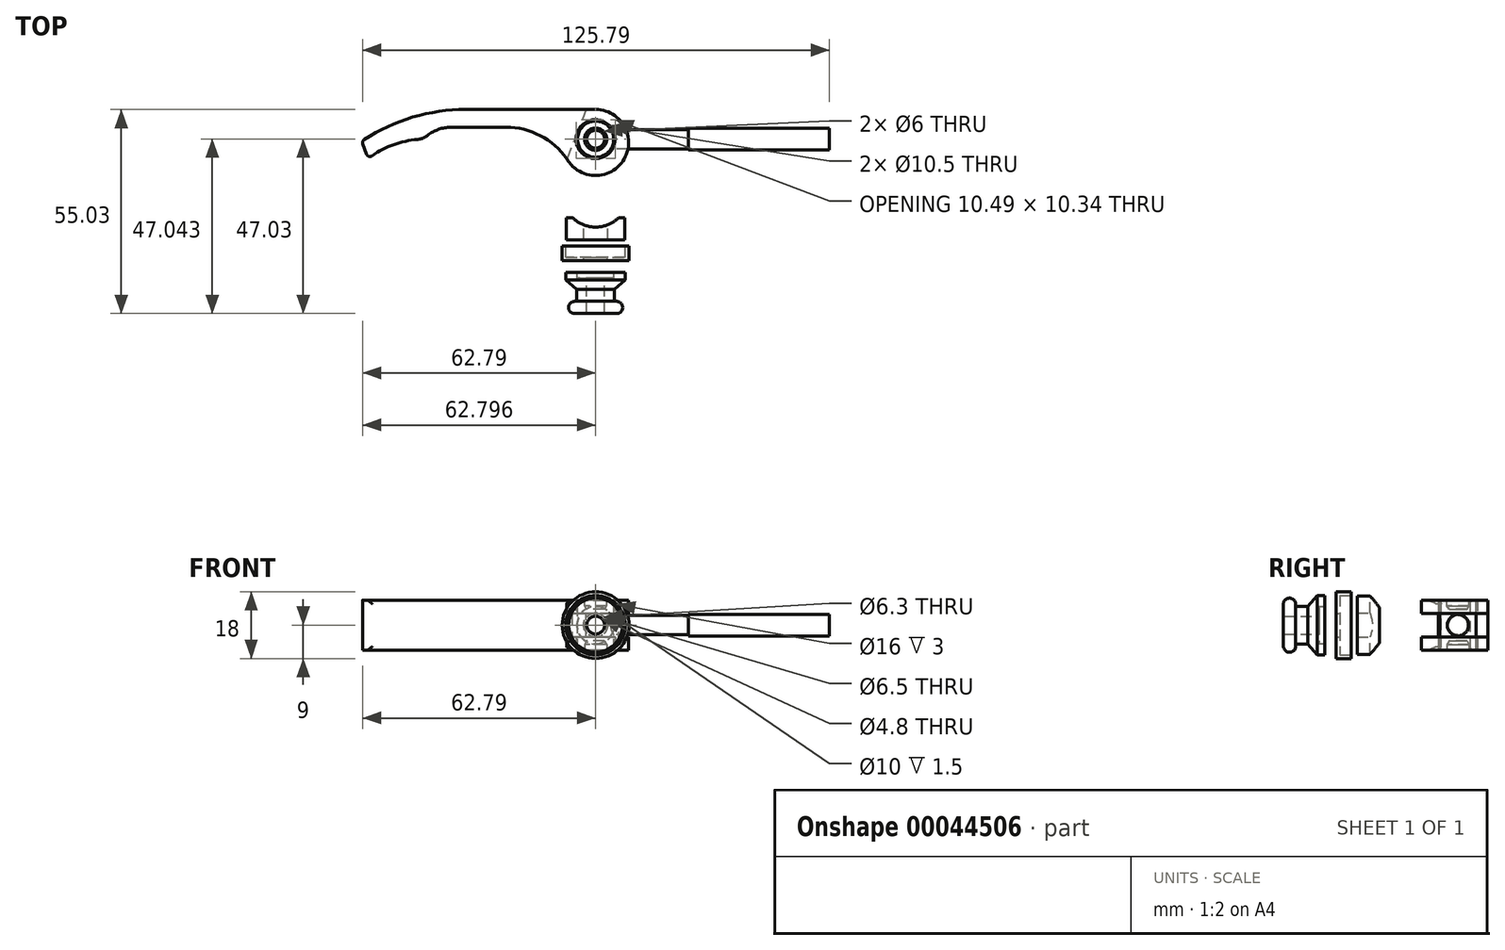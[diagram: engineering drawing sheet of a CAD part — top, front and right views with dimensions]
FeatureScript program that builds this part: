
annotation { "Feature Type Name" : "Feature", "Feature Type Description" : "" }
export const myFeature = defineFeature(function(context is Context, id is Id, definition is map)
    precondition{}
    {
        {
            var Q0;
            Q0=qCreatedBy(makeId("Top.planeOp"),FACE);
            var sketch = newSketch(context, id + "F0", { "sketchPlane" : qUnion([Q0])});
            skCircle(sketch, "E0", {"center": v(0, 0) * mm, "radius": 5.25 * mm});
            skCircle(sketch, "E1", {"center": v(0, -0.9) * mm, "radius": 8.9 * mm});
            skLineSegment(sketch, "E2", {"start": v(0, 8) * mm, "end": v(-35, 8) * mm});
            skArc(sketch, "E3", {"start": v(-35, 8) * mm, "mid": v(-49.64, 5.8) * mm, "end": v(-63, -0.58) * mm});
            skArc(sketch, "E4", {"start": v(-46.33, 0) * mm, "mid": v(-54.24, -1.42) * mm, "end": v(-61.29, -5.27) * mm});
            skArc(sketch, "E5", {"start": v(-39, 3.2) * mm, "mid": v(-43, 2.37) * mm, "end": v(-46.33, 0) * mm});
            skLineSegment(sketch, "E6", {"start": v(-63, -0.58) * mm, "end": v(-61.29, -5.27) * mm});
            skLineSegment(sketch, "E7", {"start": v(-39, 3.2) * mm, "end": v(-24.13, 3.2) * mm});
            skArc(sketch, "E8", {"start": v(-7.43, -5.8) * mm, "mid": v(-14.65, 0.8) * mm, "end": v(-24.13, 3.2) * mm});
            skLineSegment(sketch, "E9", {"start": v(-2.5, 8) * mm, "end": v(-7.74, -5.35) * mm});
            skSolve(sketch);
        }
        {
            var Q0;
            {var subQ0=sQuery(id+"F0.wireOp",EDGE,"E2");Q0=makeQuery(id+"F0.imprint","IMPRINT",FACE,{"disambiguationData":[TD([[makeQuery(id+"F0.imprint","IMPRINT",EDGE,{"derivedFrom":subQ0}),1.0]])]});}
            var Q1;
            Q1=makeQuery(id+"F0.imprint","IMPRINT",FACE,{"disambiguationData":[TD([[makeQuery(id+"F0.imprint","IMPRINT",EDGE,{"derivedFrom":sQuery(id+"F0.wireOp",EDGE,"E0")}),-1.0]])]});
            var Q2;
            {var subQ0=sQuery(id+"F0.wireOp",EDGE,"E9");var subQ1=sQuery(id+"F0.wireOp",EDGE,"E1");var subQ2=makeQuery(id+"F0.imprint","INTERSECT",VERTEX,{"disambiguationData":[OD(0.0)],"derivedFrom":[subQ1,subQ0]});Q2=makeQuery(id+"F0.imprint","IMPRINT",FACE,{"disambiguationData":[TD([[makeQuery(id+"F0.imprint","IMPRINT",EDGE,{"disambiguationData":[TD([[subQ2,-1.0]])],"derivedFrom":subQ1}),1.0]])]});}
            var Q3;
            {var subQ0=sQuery(id+"F0.wireOp",EDGE,"E3");Q3=makeQuery(id+"F0.imprint","IMPRINT",FACE,{"disambiguationData":[TD([[makeQuery(id+"F0.imprint","IMPRINT",EDGE,{"derivedFrom":subQ0}),1.0]])]});}
            extrude(context, id + "F1", {"entities" : qUnion([Q0, Q1, Q2, Q3]), "endBound" : BoundingType.SYMMETRIC, "depth" : 13.5 * mm});
        }
        {
            var Q0;
            {var subQ6=sQuery(id+"F0.wireOp",EDGE,"E0");Q0=makeQuery(id+"F0.imprint","IMPRINT",FACE,{"disambiguationData":[TD([[makeQuery(id+"F0.imprint","IMPRINT",EDGE,{"derivedFrom":subQ6}),-1.0]])]});}
            var Q1;
            Q1=makeQuery(id+"F0.imprint","IMPRINT",FACE,{"disambiguationData":[TD([[makeQuery(id+"F0.imprint","IMPRINT",EDGE,{"derivedFrom":sQuery(id+"F0.wireOp",EDGE,"E0")}),1.0]])]});
            var Q2;
            {var subQ0=sQuery(id+"F0.wireOp",EDGE,"E8");var subQ1=sQuery(id+"F0.wireOp",EDGE,"E1");var subQ2=makeQuery(id+"F0.imprint","INTERSECT",VERTEX,{"derivedFrom":[subQ1,subQ0]});Q2=makeQuery(id+"F0.imprint","IMPRINT",FACE,{"disambiguationData":[TD([[makeQuery(id+"F0.imprint","IMPRINT",EDGE,{"disambiguationData":[TD([[subQ2,1.0]])],"derivedFrom":subQ1}),-1.0]])]});}
            var Q3;
            {var subQ0=sQuery(id+"F0.wireOp",EDGE,"E2");var subQ1=sQuery(id+"F0.wireOp",EDGE,"E1");var subQ2=makeQuery(id+"F0.imprint","INTERSECT",VERTEX,{"derivedFrom":[subQ1,subQ0]});Q3=makeQuery(id+"F0.imprint","IMPRINT",FACE,{"disambiguationData":[TD([[makeQuery(id+"F0.imprint","IMPRINT",EDGE,{"disambiguationData":[TD([[subQ2,-1.0]])],"derivedFrom":subQ1}),-1.0]])]});}
            extrude(context, id + "F2", {"entities" : qUnion([Q0, Q1, Q2, Q3]), "operationType" : NewBodyOperationType.REMOVE, "endBound" : BoundingType.SYMMETRIC, "oppositeDirection" : true, "depth" : 6.4 * mm});
        }
        {
            var Q0;
            Q0=qCreatedBy(makeId("Front.planeOp"),FACE);
            var sketch = newSketch(context, id + "F3", { "sketchPlane" : qUnion([Q0])});
            skLineSegment(sketch, "E10", {"start": v(0, 14.1) * mm, "end": v(0, -21.5) * mm, "construction": true});
            skLineSegment(sketch, "E11", {"start": v(0, 0) * mm, "end": v(81.34, 0) * mm, "construction": true});
            skLineSegment(sketch, "E12.0", {"start": v(3, 6.75) * mm, "end": v(4.88, 6.75) * mm});
            skLineSegment(sketch, "E13", {"start": v(0, 4.25) * mm, "end": v(0, 0) * mm});
            skLineSegment(sketch, "E14", {"start": v(4.88, 0) * mm, "end": v(4.88, 6.75) * mm});
            skLineSegment(sketch, "E15", {"start": v(3, 6.75) * mm, "end": v(3, 5.25) * mm});
            skLineSegment(sketch, "E16", {"start": v(3, 5.25) * mm, "end": v(2.4, 4.25) * mm});
            skLineSegment(sketch, "E17", {"start": v(2.4, 4.25) * mm, "end": v(0, 4.25) * mm});
            skPoint(sketch, "E18.orphan", {"position": v(-7.73, 6.75) * mm});
            skPoint(sketch, "E19.orphan", {"position": v(8.9, 6.75) * mm});
            skLineSegment(sketch, "E20", {"start": v(0, 2.6) * mm, "end": v(25, 2.6) * mm});
            skLineSegment(sketch, "E21", {"start": v(25, 2.6) * mm, "end": v(25, 0) * mm});
            skLineSegment(sketch, "E22", {"start": v(25, 0) * mm, "end": v(0, 0) * mm});
            skLineSegment(sketch, "E23", {"start": v(25, 2.6) * mm, "end": v(25, 2.9) * mm});
            skLineSegment(sketch, "E24", {"start": v(25, 2.9) * mm, "end": v(63, 2.9) * mm});
            skLineSegment(sketch, "E25", {"start": v(63, 2.9) * mm, "end": v(63, 0) * mm});
            skLineSegment(sketch, "E26", {"start": v(63, 0) * mm, "end": v(25, 0) * mm});
            skSolve(sketch);
        }
        {
            var Q0;
            Q0=makeQuery(id+"F1.opExtrude","SWEPT_EDGE",EDGE,{"disambiguationData":[OSD([sQuery(id+"F0.wireOp",EDGE,"E4"),sQuery(id+"F0.wireOp",EDGE,"E5")])]});
            fillet(context, id + "F4", {"entities" : qUnion([Q0]), "radius" : 5 * mm, "tangentPropagation" : true, "allowEdgeOverflow" : false});
        }
        {
            var Q0;
            Q0=makeQuery(id+"F1.opExtrude","SWEPT_EDGE",EDGE,{"disambiguationData":[OSD([sQuery(id+"F0.wireOp",EDGE,"E4"),sQuery(id+"F0.wireOp",EDGE,"E6")])]});
            var Q1;
            Q1=makeQuery(id+"F1.opExtrude","SWEPT_EDGE",EDGE,{"disambiguationData":[OSD([sQuery(id+"F0.wireOp",EDGE,"E3"),sQuery(id+"F0.wireOp",EDGE,"E6")])]});
            var Q2;
            Q2=makeQuery(id+"F1.opExtrude","CAP_EDGE",EDGE,{"disambiguationData":[OSD([sQuery(id+"F0.wireOp",EDGE,"E4")])],"isStart":false});
            var Q3;
            Q3=makeQuery(id+"F1.opExtrude","CAP_EDGE",EDGE,{"disambiguationData":[OSD([sQuery(id+"F0.wireOp",EDGE,"E4")])],"isStart":true});
            fillet(context, id + "F5", {"entities" : qUnion([Q0, Q1, Q2, Q3]), "radius" : 1 * mm, "tangentPropagation" : true, "allowEdgeOverflow" : false});
        }
        {
            var Q0;
            {var subQ1=sQuery(id+"F3.wireOp",EDGE,"E12.0");Q0=makeQuery(id+"F3.imprint","IMPRINT",FACE,{"disambiguationData":[TD([[makeQuery(id+"F3.imprint","IMPRINT",EDGE,{"derivedFrom":subQ1}),-1.0]])]});}
            var Q1;
            {var subQ0=sQuery(id+"F3.wireOp",EDGE,"E22");var subQ1=sQuery(id+"F3.wireOp",EDGE,"E13");var subQ2=makeQuery(id+"F3.imprint","INTERSECT",VERTEX,{"derivedFrom":[subQ1,subQ0]});Q1=makeQuery(id+"F3.imprint","IMPRINT",FACE,{"disambiguationData":[TD([[makeQuery(id+"F3.imprint","IMPRINT",EDGE,{"disambiguationData":[TD([[subQ2,1.0]])],"derivedFrom":subQ1}),1.0]])]});}
            var Q2;
            Q2=sQuery(id+"F3.wireOp",EDGE,"E10");
            revolve(context, id + "F6", {"entities" : qUnion([Q0, Q1]), "axis" : qUnion([Q2]), "revolveType" : RevolveType.FULL});
        }
        {
            var Q0;
            Q0=makeQuery(id+"F6.opRevolve","SWEPT_BODY",BODY,{"disambiguationData":[OSD([sQuery(id+"F3.wireOp",EDGE,"E12.0"),sQuery(id+"F3.wireOp",EDGE,"E13"),sQuery(id+"F3.wireOp",EDGE,"E14"),sQuery(id+"F3.wireOp",EDGE,"E15"),sQuery(id+"F3.wireOp",EDGE,"E16"),sQuery(id+"F3.wireOp",EDGE,"E17"),sQuery(id+"F3.wireOp",EDGE,"E22")])]});
            var Q1;
            Q1=qCreatedBy(makeId("Top.planeOp"),FACE);
            mirror(context, id + "F7", {"operationType" : NewBodyOperationType.ADD, "entities" : qUnion([Q0]), "mirrorPlane" : qUnion([Q1])});
        }
        {
            var Q0;
            {var subQ5=sQuery(id+"F3.wireOp",EDGE,"E21");Q0=makeQuery(id+"F3.imprint","IMPRINT",FACE,{"disambiguationData":[TD([[makeQuery(id+"F3.imprint","IMPRINT",EDGE,{"derivedFrom":subQ5}),-1.0]])]});}
            var Q1;
            Q1=makeQuery(id+"F3.imprint","IMPRINT",FACE,{"disambiguationData":[TD([[makeQuery(id+"F3.imprint","IMPRINT",EDGE,{"derivedFrom":sQuery(id+"F3.wireOp",EDGE,"E21")}),1.0]])]});
            var Q2;
            {var subQ0=sQuery(id+"F3.wireOp",EDGE,"E22");var subQ1=sQuery(id+"F3.wireOp",EDGE,"E13");var subQ2=makeQuery(id+"F3.imprint","INTERSECT",VERTEX,{"derivedFrom":[subQ1,subQ0]});Q2=makeQuery(id+"F3.imprint","IMPRINT",FACE,{"disambiguationData":[TD([[makeQuery(id+"F3.imprint","IMPRINT",EDGE,{"disambiguationData":[TD([[subQ2,1.0]])],"derivedFrom":subQ1}),1.0]])]});}
            var Q3;
            Q3=sQuery(id+"F3.wireOp",EDGE,"E11");
            revolve(context, id + "F8", {"operationType" : NewBodyOperationType.ADD, "entities" : qUnion([Q0, Q1, Q2]), "axis" : qUnion([Q3]), "revolveType" : RevolveType.FULL});
        }
        {
            var Q0;
            Q0=qCreatedBy(makeId("Right.planeOp"),FACE);
            var sketch = newSketch(context, id + "F9", { "sketchPlane" : qUnion([Q0])});
            skLineSegment(sketch, "E27", {"start": v(-19.25, 0) * mm, "end": v(-56.74, 0) * mm, "construction": true});
            skLineSegment(sketch, "E28.bottom", {"start": v(-21.17, 7.85) * mm, "end": v(-27.17, 7.85) * mm});
            skLineSegment(sketch, "E28.top", {"start": v(-21.17, 3.25) * mm, "end": v(-27.17, 3.25) * mm});
            skLineSegment(sketch, "E28.left", {"start": v(-21.17, 7.85) * mm, "end": v(-21.17, 3.25) * mm});
            skLineSegment(sketch, "E28.right", {"start": v(-27.17, 7.85) * mm, "end": v(-27.17, 3.25) * mm});
            skLineSegment(sketch, "E29", {"start": v(-31.81, 3.15) * mm, "end": v(-31.81, 8) * mm});
            skLineSegment(sketch, "E30", {"start": v(-31.81, 8) * mm, "end": v(-28.81, 8) * mm});
            skLineSegment(sketch, "E31", {"start": v(-28.81, 8) * mm, "end": v(-28.81, 9) * mm});
            skLineSegment(sketch, "E32", {"start": v(-28.81, 9) * mm, "end": v(-32.81, 9) * mm});
            skLineSegment(sketch, "E33", {"start": v(-32.81, 9) * mm, "end": v(-32.81, 3.15) * mm});
            skLineSegment(sketch, "E34", {"start": v(-32.81, 3.15) * mm, "end": v(-31.81, 3.15) * mm});
            skLineSegment(sketch, "E35", {"start": v(-47.03, 2.4) * mm, "end": v(-47.03, 5.66) * mm});
            skLineSegment(sketch, "E36", {"start": v(-43.73, 5.66) * mm, "end": v(-43.73, 5.1) * mm});
            skLineSegment(sketch, "E37", {"start": v(-43.73, 5.1) * mm, "end": v(-40.48, 5.1) * mm});
            skLineSegment(sketch, "E38", {"start": v(-40.48, 5.1) * mm, "end": v(-37.93, 8) * mm});
            skLineSegment(sketch, "E39", {"start": v(-37.93, 8) * mm, "end": v(-35.93, 8) * mm});
            skLineSegment(sketch, "E40", {"start": v(-35.93, 8) * mm, "end": v(-35.93, 5) * mm});
            skLineSegment(sketch, "E41", {"start": v(-35.93, 5) * mm, "end": v(-37.43, 5) * mm});
            skLineSegment(sketch, "E42", {"start": v(-37.43, 5) * mm, "end": v(-37.43, 2.4) * mm});
            skLineSegment(sketch, "E43", {"start": v(-37.43, 2.4) * mm, "end": v(-47.03, 2.4) * mm});
            skArc(sketch, "E44", {"start": v(-43.73, 5.66) * mm, "mid": v(-45.38, 7.31) * mm, "end": v(-47.03, 5.66) * mm});
            skSolve(sketch);
        }
        {
            var Q0;
            Q0=makeQuery(id+"F9.imprint","IMPRINT",FACE,{"disambiguationData":[TD([[makeQuery(id+"F9.imprint","IMPRINT",EDGE,{"derivedFrom":sQuery(id+"F9.wireOp",EDGE,"E28.bottom")}),1.0]])]});
            var Q1;
            Q1=makeQuery(id+"F9.imprint","IMPRINT",FACE,{"disambiguationData":[TD([[makeQuery(id+"F9.imprint","IMPRINT",EDGE,{"derivedFrom":sQuery(id+"F9.wireOp",EDGE,"E29")}),1.0]])]});
            var Q2;
            Q2=makeQuery(id+"F9.imprint","IMPRINT",FACE,{"disambiguationData":[TD([[makeQuery(id+"F9.imprint","IMPRINT",EDGE,{"derivedFrom":sQuery(id+"F9.wireOp",EDGE,"E35")}),-1.0]])]});
            var Q3;
            Q3=sQuery(id+"F9.wireOp",EDGE,"E27");
            revolve(context, id + "F10", {"entities" : qUnion([Q0, Q1, Q2]), "axis" : qUnion([Q3]), "revolveType" : RevolveType.FULL});
        }
        {
            var Q0;
            Q0=qCreatedBy(makeId("Top.planeOp"),FACE);
            var sketch = newSketch(context, id + "F11", { "sketchPlane" : qUnion([Q0])});
            skLineSegment(sketch, "E45.0", {"start": v(-7.85, -21.17) * mm, "end": v(7.85, -21.17) * mm});
            skArc(sketch, "E46", {"start": v(-6.24, -21.17) * mm, "mid": v(0, -23.72) * mm, "end": v(6.24, -21.17) * mm});
            skSolve(sketch);
        }
        {
            var Q0;
            Q0 = qSketchRegion(id + "F11", true);
            extrude(context, id + "F12", {"entities" : qUnion([Q0]), "operationType" : NewBodyOperationType.REMOVE, "endBound" : BoundingType.THROUGH_ALL, "oppositeDirection" : true, "depth" : 25 * mm, "hasSecondDirection" : true, "secondDirectionBound" : SecondDirectionBoundingType.THROUGH_ALL, "secondDirectionOppositeDirection" : false, "secondDirectionDepth" : 25 * mm});
        }
    });
